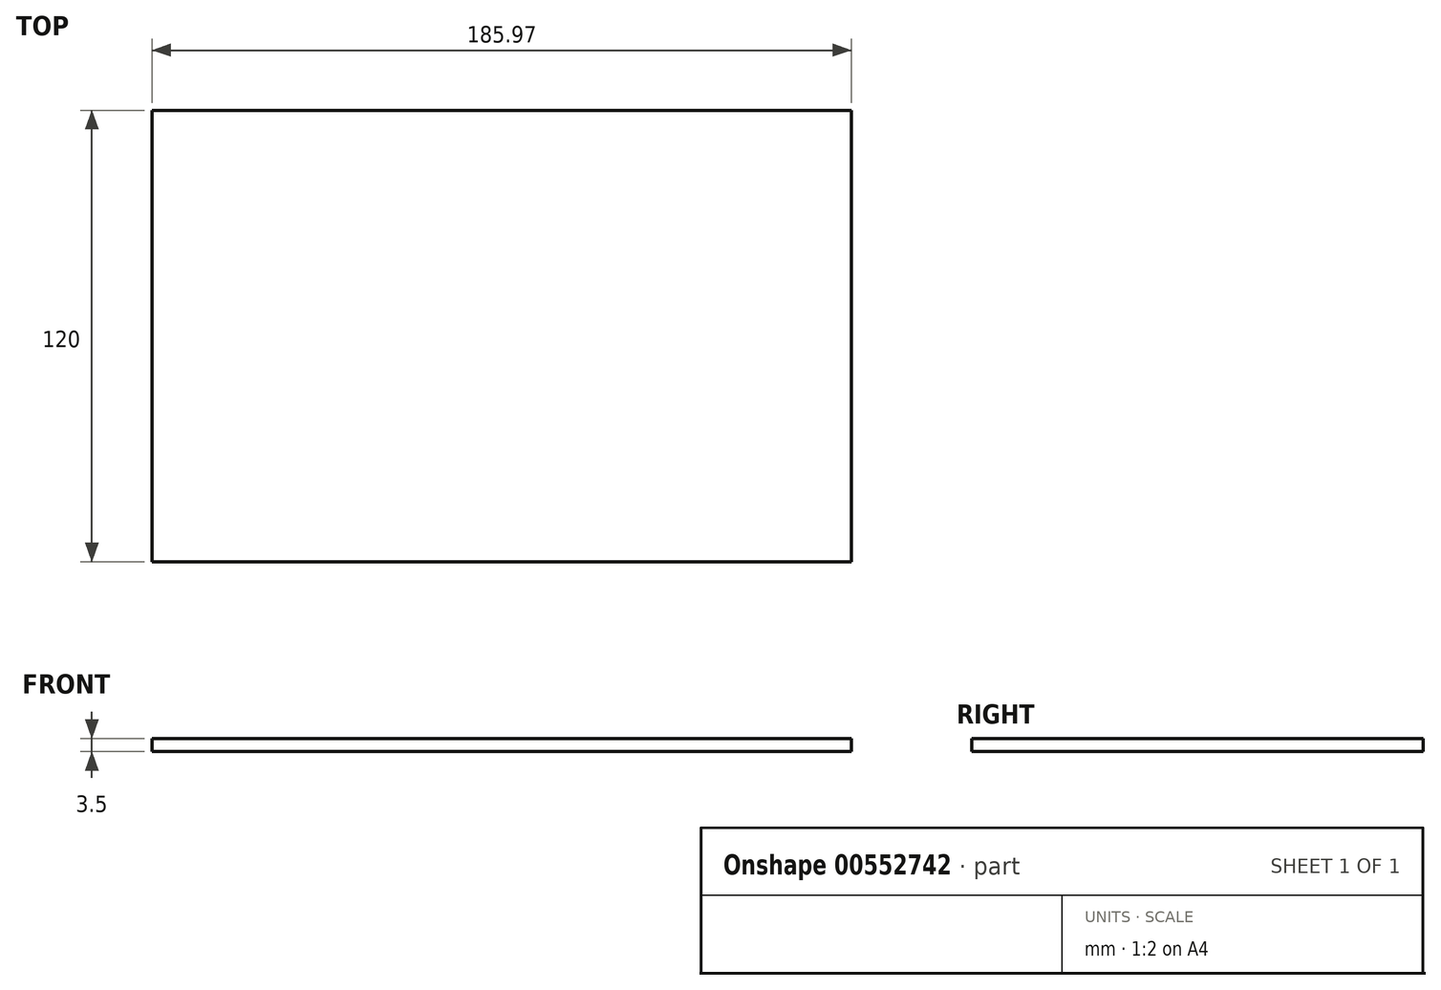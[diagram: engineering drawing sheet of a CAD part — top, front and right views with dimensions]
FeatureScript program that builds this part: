
annotation { "Feature Type Name" : "Feature", "Feature Type Description" : "" }
export const myFeature = defineFeature(function(context is Context, id is Id, definition is map)
    precondition{}
    {
        {
            var Q0;
            Q0=qCreatedBy(makeId("Top.planeOp"),FACE);
            var sketch = newSketch(context, id + "F0", { "sketchPlane" : qUnion([Q0])});
            skLineSegment(sketch, "E0.bottom", {"start": v(0, 81.63) * mm, "end": v(-185.97, 81.63) * mm});
            skLineSegment(sketch, "E0.top", {"start": v(0, -38.37) * mm, "end": v(-185.97, -38.37) * mm});
            skLineSegment(sketch, "E0.left", {"start": v(0, 81.63) * mm, "end": v(0, -38.37) * mm});
            skLineSegment(sketch, "E0.right", {"start": v(-185.97, 81.63) * mm, "end": v(-185.97, -38.37) * mm});
            skSolve(sketch);
        }
        {
            var Q0;
            Q0=makeQuery(id+"F0.imprint","IMPRINT",FACE,{"disambiguationData":[TD([[makeQuery(id+"F0.imprint","IMPRINT",EDGE,{"derivedFrom":sQuery(id+"F0.wireOp",EDGE,"E0.bottom")}),1.0]])]});
            extrude(context, id + "F1", {"entities" : qUnion([Q0]), "depth" : 3.5 * mm, "offsetDistance" : 25 * mm});
        }
        {
            var Q0;
            Q0=makeQuery(id+"F1.opExtrude","CAP_FACE",FACE,{"disambiguationData":[OSD([sQuery(id+"F0.wireOp",EDGE,"E0.bottom"),sQuery(id+"F0.wireOp",EDGE,"E0.top"),sQuery(id+"F0.wireOp",EDGE,"E0.left"),sQuery(id+"F0.wireOp",EDGE,"E0.right")])],"isStart":false});
            var sketch = newSketch(context, id + "F2", { "sketchPlane" : qUnion([Q0])});
            skSolve(sketch);
        }
        {
            var Q0;
            Q0=qCreatedBy(makeId("Top.planeOp"),FACE);
            var sketch = newSketch(context, id + "F3", { "sketchPlane" : qUnion([Q0])});
            skText(sketch, "E1", { "text": "joyeux\n", "fontName": "OpenSans-Regular.ttf"});
            const initialGuessF3  = {"E1": [-0.14075, 0.04786, 1, 0, 0.02]};
            skSetInitialGuess(sketch, initialGuessF3);
            skSolve(sketch);
        }
        {
            var Q0;
            Q0=makeQuery(id+"F2.imprint","IMPRINT",FACE,{"disambiguationData":[TD([[makeQuery(id+"F2.imprint","IMPRINT",EDGE,{"derivedFrom":makeQuery(id+"F1.opExtrude","CAP_EDGE",EDGE,{"disambiguationData":[OSD([sQuery(id+"F0.wireOp",EDGE,"E0.bottom")])],"isStart":false})}),1.0]])]});
            var sketch = newSketch(context, id + "F4", { "sketchPlane" : qUnion([Q0])});
            skText(sketch, "E2", { "text": "anniversaire\n", "fontName": "OpenSans-Regular.ttf"});
            const initialGuessF4  = {"E2": [-0.17272, 0, 1, 0, 0.02]};
            skSetInitialGuess(sketch, initialGuessF4);
            skSolve(sketch);
        }
        {
            var Q0;
            Q0 = qSketchRegion(id + "F3", true);
            extrude(context, id + "F5", {"entities" : qUnion([Q0]), "operationType" : NewBodyOperationType.REMOVE, "endBound" : BoundingType.THROUGH_ALL, "oppositeDirection" : true, "depth" : 25 * mm, "offsetDistance" : 25 * mm});
        }
    });
